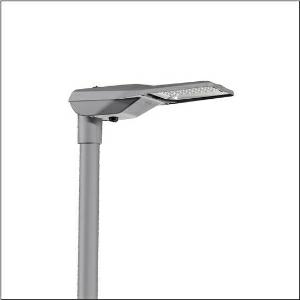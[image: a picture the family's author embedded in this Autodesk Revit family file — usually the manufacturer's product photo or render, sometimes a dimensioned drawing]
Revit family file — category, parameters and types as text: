
# Revit family: streetlight_sl_21_iq_mini___st1_0a_5xe2d51y08jb_5dfa
name_source: partatom
category: Lighting Fixtures
units: mm (PartAtom-declared; Revit-internal decimal feet)

## family parameters
Cut with Voids When Loaded = No
Host = Face
Light Source = No
Part Type = Normal
Room Calculation Point = No
Round Connector Dimension = Use Diameter
Shared = No

## types (1)
- --- (1 x LED, 9850 lm, 72.5 W, 3000K)
    Apparent Load = 73 VA
    CIE Flux Codes = 40 73 97 100 100
    Color Rendering = 80
    Color Temperature = 3000K
    Default Elevation = 1800 mm
    Description = Streetlight SL 21 iQ mini, mast luminaire, primary light control with lens, of PMMA, primary optical cover: cover, of toughened safety glass, transparent, light distribution: ST1.0a, light emission: direct distribution, primary light characteristic: asymmetric, installation type: post-top, side-entry, LED, High Power LED, rated luminous flux: 9.850lm, luminous efficacy: 136lm/W, light colour: 830, colour temperature: 3000K, control gear: iQ-Street Remote, D4i with power reduction, control: pre-setting: logarithmic dimming characteristic, Street-Remote, Auto-Match, Temp-Guard, Lumen-Switch, Night-Set, Smart-Wire, Light-Fading, Desk-Remote (wireless, voltage-free reading and setting of iQ features in the workshop via application-optimized NFC function/RFID function), optimised constant luminous flux control (CLO 2.0), mains connection: 220..240V, AC, 50/60Hz, start of lifetime: 73W, end of service life: 76W, reduction: 33W, luminaire housing, of diecast aluminium, powder-coated, Siteco® metallic grey (DB 702S), corrosivity category C5 mid according to DIN EN ISO 12944, please order mast flange separately, inclination adjustable: 0°, 5°, 10°, 15°, sealing non-destructively replaceable, multi-level sealing system, length: 628mm, width: 235mm, height: 110mm, mast flange for spigot size: 42mm (side-entry): 5XC10008XM4, 60/48mm (side-entry/post-top): 5XC10108XM2, 76/60mm (side-entry/post-top): 5XC10108XM1, mounting height: 4..8m, Smart Interface below and above, protection rating (complete): IP66, insulation class (complete): insulation class II (safety insulation), certification: CE, ENEC, ENEC+, VDE, impact resistance: IK10, permissible operating ambient temperature for outdoor applications: -40..+50°C, standard-compliant lighting for roads and squares, packaging unit: 1 piece

Light Distribution: ST1.0a
    Height = 110 mm
    Lamp = 1 x LED
    Lamp Light Flux = 9850 lm
    Lamp Power = 72.5 W
    Lamp count = 1
    Length = 625 mm
    Luminous efficacy = 136 lm/W
    Manufacturer = Siteco
    ModVariant = No
    Model = 5XE2D51Y08JB
    Number of Poles = 1
    OnlyDefault = Yes
    Power Factor = 1
    Product Name = Streetlight SL 21 iQ mini | ST1.0a
    Product group = mast luminaire | pylon top
    ProductGroupID = 6100
    Protection Class = Protection class II
    Protection Degree = IP 66
    RLX_Detail_Level = 1
    RLX_Emergency_Light_Flux = 0 lm
    RLX_Emergency_Type = 0
    RLX_Emergency_Type_DB = No
    RlxData = <blob elided: 26665 chars, md5=6f2e9db8>
    Socket = socket
    Standby Power = 0 W
    System Light Flux = 9850 lm
    System Power = 73 W
    Type Comments = factory setting: luminous flux: 100 % | dim-lin: 254 | 755 mA
    Type Image = l_1003514.jpg
    URL = http://relux.com
    VarID = @adj_114034
    Voltage = 0 V
    Weight = 0.00 kg
    Width = 234 mm

## geometry (parser evidence)
native form markers: Blend x4, Sweep x13
no freeform markers — native parametric forms only
